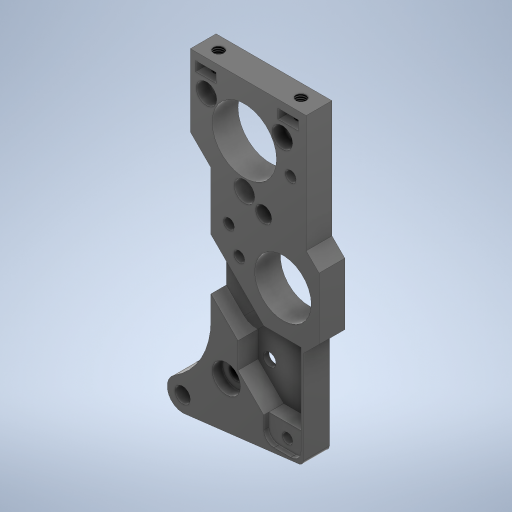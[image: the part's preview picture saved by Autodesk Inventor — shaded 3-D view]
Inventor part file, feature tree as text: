
AUTODESK INVENTOR PART (.ipt)
format: ipt  version: 2023 (Build 270158000, 158)  size: 720,384 bytes
history: native  units: mm
features: extrude x16, sketch x11, fillet x5, projected_geometry x5, thread x2, chamfer x1
ambient origin geometry x8: Origin, YZ Plane, XZ Plane, XY Plane, X Axis, Y Axis, Z Axis, Center Point
bodies: Solid1 (feature_tree)
feature tree (40):
  extrude  "Extrusion1"  Depth=6.0mm
  fillet  "Fillet1"  Radius=23.5mm
  fillet  "Fillet2"  Radius=6.0mm
  extrude  "Extrusion2"  Depth=3.0mm
  extrude  "Extrusion3"  Depth=56.0mm
  thread  "Thread1"  [1 undecoded]
  thread  "Thread2"  [1 undecoded]
  sketch  "Sketch5"  dims[d4=0.0mm d5=3.0mm]
  extrude  "Extrusion4"  Depth=12.5mm
  extrude  "Extrusion5"  Depth=2.1mm
  extrude  "Extrusion6"  Depth=4.0mm
  extrude  "Extrusion7"  TaperAngle=45.0deg  [1 undecoded]
  extrude  "Extrusion8"  Depth=12.0mm
  extrude  "Extrusion9"  TaperAngle=135.0deg  [1 undecoded]
  extrude  "Extrusion10"  Depth=5.0mm TaperAngle=0.0deg
  fillet  "Fillet3"  Radius=3.0mm
  extrude  "Extrusion11"  Depth=10.0mm
  chamfer  "Chamfer1"  Distance=2.5mm
  fillet  "Fillet4"  Radius=13.5mm
  extrude  "Extrusion12"  Depth=10.0mm
  extrude  "Extrusion13"  Depth=10.0mm
  extrude  "Extrusion14"  Depth=10.0mm
  fillet  "Fillet5"  Radius=12.5mm
  extrude  "Extrusion15"  Depth=10.0mm
  extrude  "Extrusion16"  Depth=10.0mm
  sketch  "Sketch3"  dims[d0=3.0mm d1=6.0mm d2=23.5mm d3=6.0mm]
  projected_geometry  "Projected Loop1"
  sketch  "Sketch7"  dims[d6=18.0mm d7=56.0mm d8=11.0mm d9=4.0mm]
  sketch  "Sketch8"  dims[d10=24.75mm d11=12.5mm]
  projected_geometry  "Projected Loop2"
  sketch  "Sketch10"  dims[d12=22.3mm d14=2.1mm]
  sketch  "Sketch13"  dims[d18=30.0mm d20=360.0deg d22=4.0mm]
  sketch  "Sketch15"  dims[d23=14.0mm d24=45.0deg]
  sketch  "Sketch17"  dims[d25=3.0mm d26=12.0mm]
  projected_geometry  "Projected Loop3"
  sketch  "Sketch21"  dims[d27=6.0mm d28=135.0deg]
  projected_geometry  "Projected Loop5"
  sketch  "Sketch22"  dims[d29=135.0deg d30=5.0mm d31=0.0mm d32=3.0mm]
  projected_geometry  "Projected Loop6"
  sketch  "Sketch24"  dims[d33=10.0mm d34=3.0mm d35=2.5mm d36=13.5mm d37=7.5mm d38=2.5mm d39=15.0mm d40=12.5mm d41=1.0mm d42=15.0mm d43=12.75mm d44=20.0mm d45=23.75mm d46=3.0mm d47=0.0mm d48=2.0mm d49=2.0mm d50=2.5mm d51=2.5mm d52=3.0mm d53=3.0mm d54=4.5mm d55=0.0mm d56=7.0mm d57=0.0mm d58=7.0mm d59=0.0mm d60=8.5mm d61=270.0deg d62=4.0mm d63=4.0mm d64=4.0mm d65=3.0mm d66=0.0mm d67=5.5mm d68=2.0mm d69=0.0mm d70=4.0mm d71=1.85mm d72=4.0mm d73=1.85mm d74=1.0mm d75=2.425mm d76=2.425mm d77=1.0mm d78=10.0mm d79=0.0mm d82=3.1mm d83=11.15mm d84=2.1mm d85=2.1mm d86=2.1mm d87=5.5mm d88=3.5mm d89=25.75mm d90=30.25mm d91=2.5mm d92=11.75mm d93=24.0mm d94=8.0mm d95=2.1mm d96=2.1mm d98=2.1mm d99=1.8mm d100=0.0mm d101=2.1mm d102=2.1mm d103=2.1mm d104=1.8mm d105=0.0mm d117=3.9mm d118=0.0mm d119=18.0mm d120=6.5mm d121=0.0mm d122=1.0mm d125=5.0mm d126=7.25mm d127=2.5mm d128=5.0mm d129=15.0mm d130=5.0mm d131=5.0mm d132=90.0deg d133=135.0deg d135=135.0deg d136=135.0deg d137=3.0mm d138=0.0mm d139=0.9mm d140=2.0mm d141=45.0deg d142=4.0mm d143=2.0mm d144=2.6mm d145=3.625mm d146=10.0mm d147=0.0mm d148=2.05mm d149=2.4mm d150=0.0mm d151=4.5mm d154=1.0mm d155=0.0mm d156=2.0mm d157=2.8mm d158=0.5mm d159=10.0mm d160=0.0mm d161=2.5mm d162=0.0mm d80=0.5mm d81=0.872665mm d106=0.872665mm d123=0.872665mm d134=0.5mm d153=0.5mm]
note: 4 required parameter values undecoded (feature->parameter linkage not recoverable at this tier; creation-order binding heuristic only, values carry confidence <= 0.55)
